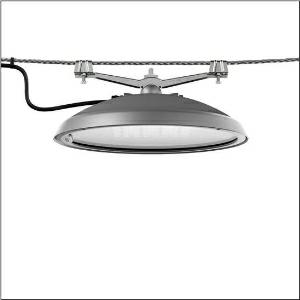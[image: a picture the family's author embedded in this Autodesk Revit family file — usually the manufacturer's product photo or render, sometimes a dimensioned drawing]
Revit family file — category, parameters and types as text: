
# Revit family: dl_50_iq_mini___st0_8s_5xa248v41f08fe_9c34
name_source: partatom
category: Lighting Fixtures
units: mm (PartAtom-declared; Revit-internal decimal feet)

## family parameters
Cut with Voids When Loaded = No
Host = Face
Light Source = No
Part Type = Normal
Room Calculation Point = No
Round Connector Dimension = Use Diameter
Shared = No

## types (1)
- --- (1 x LED, 2690 lm, 15.7 W, 4000K)
    Apparent Load = 16 VA
    CIE Flux Codes = 38 75 97 100 100
    Color Rendering = 70
    Color Temperature = 4000K
    Default Elevation = 1800 mm
    Description = DL 50 iQ mini, catenary luminaire, primary light control with lens, of PMMA, primary optical cover: cover, of toughened safety glass, transparent, light distribution: ST0.8s, light emission: direct distribution, primary light characteristic: symmetric, installation type: suspended mounting, LED, High Power LED, rated luminous flux: 2.690lm, luminous efficacy: 171lm/W, light colour: 740, colour temperature: 4000K, control gear: iQ Street-Remote, control: optimised constant luminous flux control (CLO 2.0), Desk-Remote (wireless, voltage-free reading and setting of iQ features in the workshop via application-optimized NFC function/RFID function), Light-Fading, Smart-Wire, Night-Set, Lumen-Switch, Temp-Guard, Auto-Match, Street-Remote, mains connection: 230..240V, AC, 50/60Hz, start of lifetime: 16W, end of service life: 16W, reduction: 8W, luminaire housing, of diecast aluminium, powder-coated, SITECO metallic grey (DB 702S), diameter: 500mm, height: 115mm, mounting height: 4..12m, protection rating (complete): IP66, insulation class (complete): insulation class II (safety insulation), certification: CE, ENEC, ENEC+, VDE, impact resistance: IK08, permissible operating ambient temperature for outdoor applications: -25..+40°C, standard-compliant lighting for roads and squares, packaging unit: 1 piece

Light Distribution: ST0.8s
    Height = 124 mm  [stored 0.406824 ft]
    Lamp = 1 x LED
    Lamp Light Flux = 2690 lm
    Lamp Power = 15.7 W
    Lamp count = 1
    Length = 500 mm
    Luminous efficacy = 171 lm/W
    Manufacturer = Siteco
    ModVariant = No
    Model = 5XA248V41F08FE
    Number of Poles = 1
    OnlyDefault = Yes
    Power Factor = 1
    Product Name = DL 50 iQ mini | ST0.8s
    Product group = catenary luminaire
    ProductGroupID = 6300
    Protection Class = Protection class II
    Protection Degree = IP 66
    RLX_Detail_Level = 1
    RLX_Emergency_Light_Flux = 0 lm
    RLX_Emergency_Type = 0
    RLX_Emergency_Type_DB = No
    RlxData = <blob elided: 123013 chars, md5=0a7ff794>
    Socket = socket
    Standby Power = 0 W
    System Light Flux = 2690 lm
    System Power = 16 W
    Type Comments = factory setting: luminous flux: 100 % | dim-lin: 254 | 319 mA
    Type Image = l_1242791.jpg
    URL = http://relux.com
    VarID = @adj_137427
    Voltage = 0 V
    Weight = 0.00 kg
    Width = 0 mm  [stored 0 ft]

note: [stored X ft] marks values corroborated as IEEE doubles in the binary element streams (Revit-internal decimal feet)

## geometry (parser evidence)
native form markers: Blend x4, Sweep x12
no freeform markers — native parametric forms only
